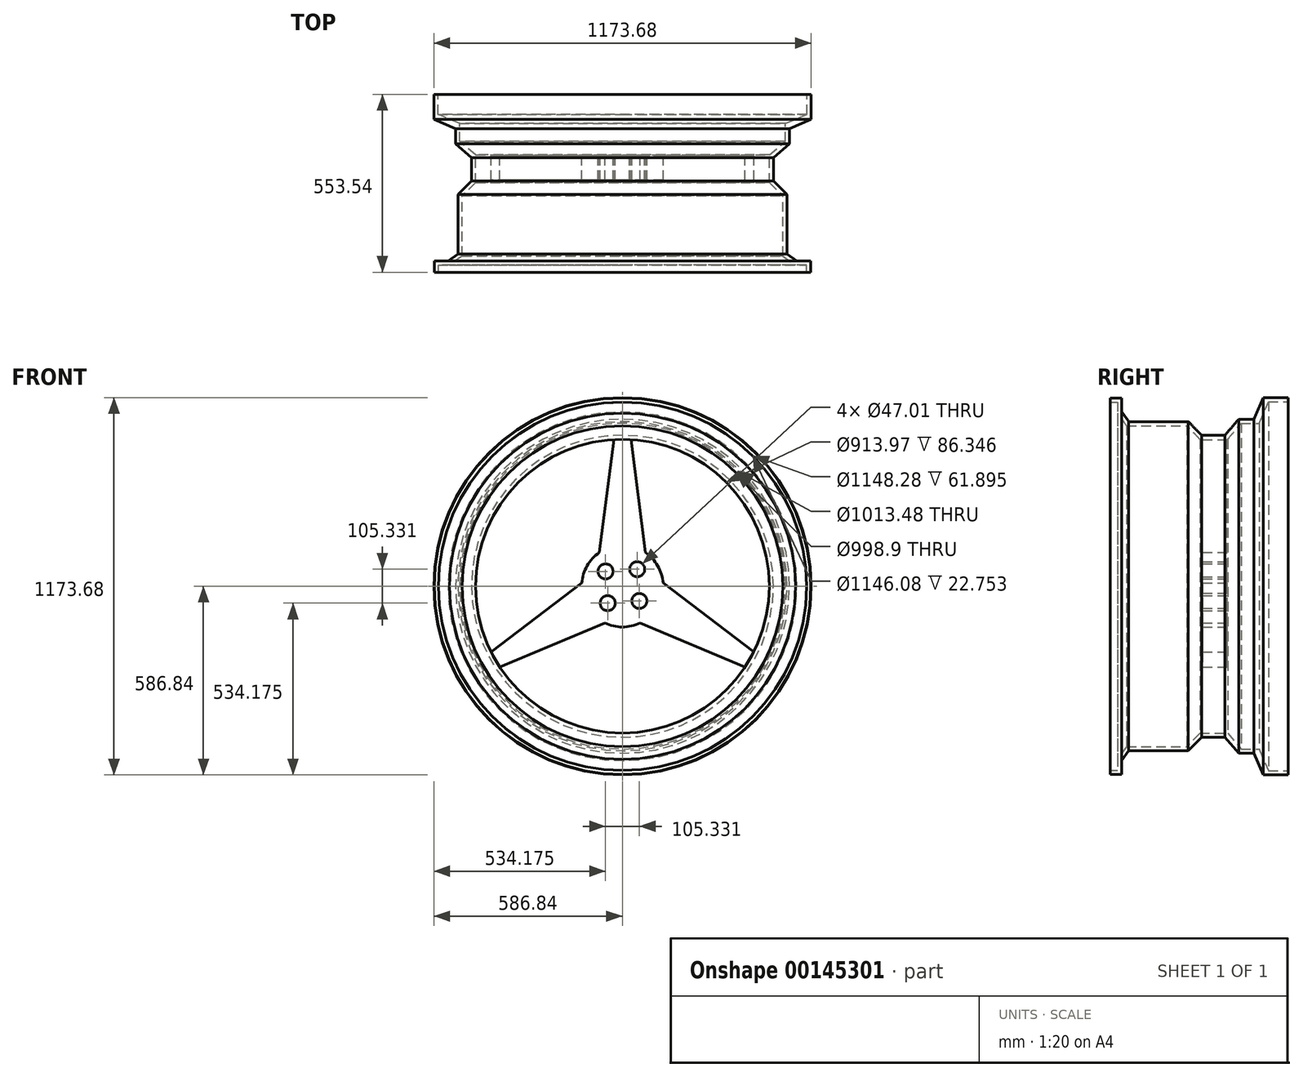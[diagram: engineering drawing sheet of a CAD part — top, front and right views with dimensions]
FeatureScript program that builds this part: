
annotation { "Feature Type Name" : "Feature", "Feature Type Description" : "" }
export const myFeature = defineFeature(function(context is Context, id is Id, definition is map)
    precondition{}
    {
        {
            var Q0;
            Q0=qCreatedBy(makeId("Top.planeOp"),FACE);
            var sketch = newSketch(context, id + "F0", { "sketchPlane" : qUnion([Q0])});
            skLineSegment(sketch, "E0", {"start": v(585.74, -553.54) * mm, "end": v(585.74, -518.09) * mm});
            skLineSegment(sketch, "E1", {"start": v(585.74, -518.09) * mm, "end": v(542.43, -518.09) * mm});
            skLineSegment(sketch, "E2", {"start": v(469.68, -197.1) * mm, "end": v(519.44, -154.49) * mm});
            skLineSegment(sketch, "E3", {"start": v(519.44, -154.49) * mm, "end": v(519.44, -107.02) * mm});
            skLineSegment(sketch, "E4", {"start": v(573.04, -530.79) * mm, "end": v(538.37, -530.79) * mm});
            skLineSegment(sketch, "E5", {"start": v(456.98, -188.76) * mm, "end": v(506.74, -146.9) * mm});
            skLineSegment(sketch, "E6", {"start": v(506.74, -146.9) * mm, "end": v(506.74, -90.85) * mm});
            skLineSegment(sketch, "E7", {"start": v(519.44, -107.02) * mm, "end": v(586.84, -77.36) * mm});
            skLineSegment(sketch, "E8", {"start": v(586.84, -77.36) * mm, "end": v(586.84, 0) * mm});
            skLineSegment(sketch, "E9", {"start": v(506.74, -90.85) * mm, "end": v(574.14, -61.9) * mm});
            skLineSegment(sketch, "E10", {"start": v(574.14, -61.9) * mm, "end": v(574.14, 0) * mm});
            skLineSegment(sketch, "E11", {"start": v(573.04, -553.54) * mm, "end": v(573.04, -530.79) * mm});
            skLineSegment(sketch, "E12", {"start": v(469.68, -197.1) * mm, "end": v(469.68, -269.98) * mm});
            skLineSegment(sketch, "E13", {"start": v(456.98, -188.76) * mm, "end": v(456.98, -275.1) * mm});
            skLineSegment(sketch, "E14", {"start": v(456.98, -275.1) * mm, "end": v(499.45, -315.5) * mm});
            skLineSegment(sketch, "E15", {"start": v(499.45, -315.5) * mm, "end": v(499.45, -503.08) * mm});
            skLineSegment(sketch, "E16", {"start": v(499.45, -503.08) * mm, "end": v(538.37, -530.79) * mm});
            skLineSegment(sketch, "E17", {"start": v(542.43, -518.09) * mm, "end": v(512.15, -496.53) * mm});
            skLineSegment(sketch, "E18", {"start": v(512.15, -496.53) * mm, "end": v(512.15, -311.07) * mm});
            skLineSegment(sketch, "E19", {"start": v(512.15, -311.07) * mm, "end": v(469.68, -269.98) * mm});
            skLineSegment(sketch, "E20", {"start": v(574.14, 0) * mm, "end": v(586.84, 0) * mm});
            skLineSegment(sketch, "E21", {"start": v(585.74, -553.54) * mm, "end": v(573.04, -553.54) * mm});
            skLineSegment(sketch, "E22", {"start": v(0, 0) * mm, "end": v(0, -115.18) * mm});
            skSolve(sketch);
        }
        {
            var Q0;
            Q0=makeQuery(id+"F0.imprint","IMPRINT",FACE,{"disambiguationData":[TD([[makeQuery(id+"F0.imprint","IMPRINT",EDGE,{"derivedFrom":sQuery(id+"F0.wireOp",EDGE,"E0")}),1.0]])]});
            var Q1;
            Q1=sQuery(id+"F0.wireOp",EDGE,"E22");
            revolve(context, id + "F1", {"entities" : qUnion([Q0]), "axis" : qUnion([Q1]), "revolveType" : RevolveType.FULL});
        }
        {
            var Q0;
            Q0=qCreatedBy(makeId("Front.planeOp"),FACE);
            cPlane(context, id + "F2", {"entities" : qUnion([Q0]), "cplaneType" : CPlaneType.OFFSET, "offset" : 190.5 * mm, "width" : 152.4 * mm, "height" : 152.4 * mm});
        }
        {
            var Q0;
            Q0=qCreatedBy(id+"F2.planeOp",FACE);
            var sketch = newSketch(context, id + "F3", { "sketchPlane" : qUnion([Q0])});
            skCircle(sketch, "E23", {"center": v(0, 0) * mm, "radius": 127 * mm});
            skCircle(sketch, "E24.0", {"center": v(0, 0) * mm, "radius": 456.98 * mm});
            skCircle(sketch, "E25", {"center": v(0, 0) * mm, "radius": 457.17 * mm});
            skLineSegment(sketch, "E26", {"start": v(0, 127) * mm, "end": v(0, 456.98) * mm});
            skLineSegment(sketch, "E27", {"start": v(-71.66, 104.85) * mm, "end": v(-26.93, 456.38) * mm});
            skLineSegment(sketch, "E28.MirrorCS", {"start": v(71.66, 104.85) * mm, "end": v(26.93, 456.38) * mm});
            skLineSegment(sketch, "E29.1.0", {"start": v(-54.98, -114.48) * mm, "end": v(-381.77, -251.51) * mm});
            skLineSegment(sketch, "E29.1.1", {"start": v(-126.63, 9.63) * mm, "end": v(-408.7, -204.87) * mm});
            skLineSegment(sketch, "E29.2.0", {"start": v(126.63, 9.63) * mm, "end": v(408.7, -204.87) * mm});
            skLineSegment(sketch, "E29.2.1", {"start": v(54.98, -114.48) * mm, "end": v(381.77, -251.51) * mm});
            skCircle(sketch, "E30", {"center": v(-52.67, 45.9) * mm, "radius": 23.5 * mm});
            skCircle(sketch, "E31.1.0", {"center": v(-45.9, -52.67) * mm, "radius": 23.5 * mm});
            skCircle(sketch, "E31.2.0", {"center": v(52.67, -45.9) * mm, "radius": 23.5 * mm});
            skCircle(sketch, "E31.3.0", {"center": v(45.9, 52.67) * mm, "radius": 23.5 * mm});
            skSolve(sketch);
        }
        {
            var Q0;
            {var subQ0=sQuery(id+"F3.wireOp",EDGE,"E29.1.0");var subQ1=sQuery(id+"F3.wireOp",EDGE,"E23");var subQ2=makeQuery(id+"F3.imprint","INTERSECT",VERTEX,{"derivedFrom":[subQ1,subQ0]});Q0=makeQuery(id+"F3.imprint","IMPRINT",FACE,{"disambiguationData":[TD([[makeQuery(id+"F3.imprint","IMPRINT",EDGE,{"disambiguationData":[TD([[subQ2,1.0]])],"derivedFrom":subQ1}),-1.0]])]});}
            var Q1;
            {var subQ0=sQuery(id+"F3.wireOp",EDGE,"E26");Q1=makeQuery(id+"F3.imprint","IMPRINT",FACE,{"disambiguationData":[TD([[makeQuery(id+"F3.imprint","IMPRINT",EDGE,{"derivedFrom":subQ0}),1.0]])]});}
            var Q2;
            {var subQ0=sQuery(id+"F3.wireOp",EDGE,"E26");Q2=makeQuery(id+"F3.imprint","IMPRINT",FACE,{"disambiguationData":[TD([[makeQuery(id+"F3.imprint","IMPRINT",EDGE,{"derivedFrom":subQ0}),-1.0]])]});}
            var Q3;
            {var subQ0=sQuery(id+"F3.wireOp",EDGE,"E29.2.0");var subQ1=sQuery(id+"F3.wireOp",EDGE,"E23");var subQ2=makeQuery(id+"F3.imprint","INTERSECT",VERTEX,{"derivedFrom":[subQ1,subQ0]});Q3=makeQuery(id+"F3.imprint","IMPRINT",FACE,{"disambiguationData":[TD([[makeQuery(id+"F3.imprint","IMPRINT",EDGE,{"disambiguationData":[TD([[subQ2,1.0]])],"derivedFrom":subQ1}),-1.0]])]});}
            var Q4;
            {var subQ0=sQuery(id+"F3.wireOp",EDGE,"E23");var subQ4=makeQuery(id+"F3.imprint","INTERSECT",VERTEX,{"derivedFrom":[subQ0,sQuery(id+"F3.wireOp",EDGE,"E28.MirrorCS")]});Q4=makeQuery(id+"F3.imprint","IMPRINT",FACE,{"disambiguationData":[TD([[makeQuery(id+"F3.imprint","IMPRINT",EDGE,{"disambiguationData":[TD([[subQ4,1.0]])],"derivedFrom":subQ0}),1.0]])]});}
            extrude(context, id + "F4", {"entities" : qUnion([Q0, Q1, Q2, Q3, Q4]), "operationType" : NewBodyOperationType.ADD, "depth" : 76.2 * mm});
        }
    });
